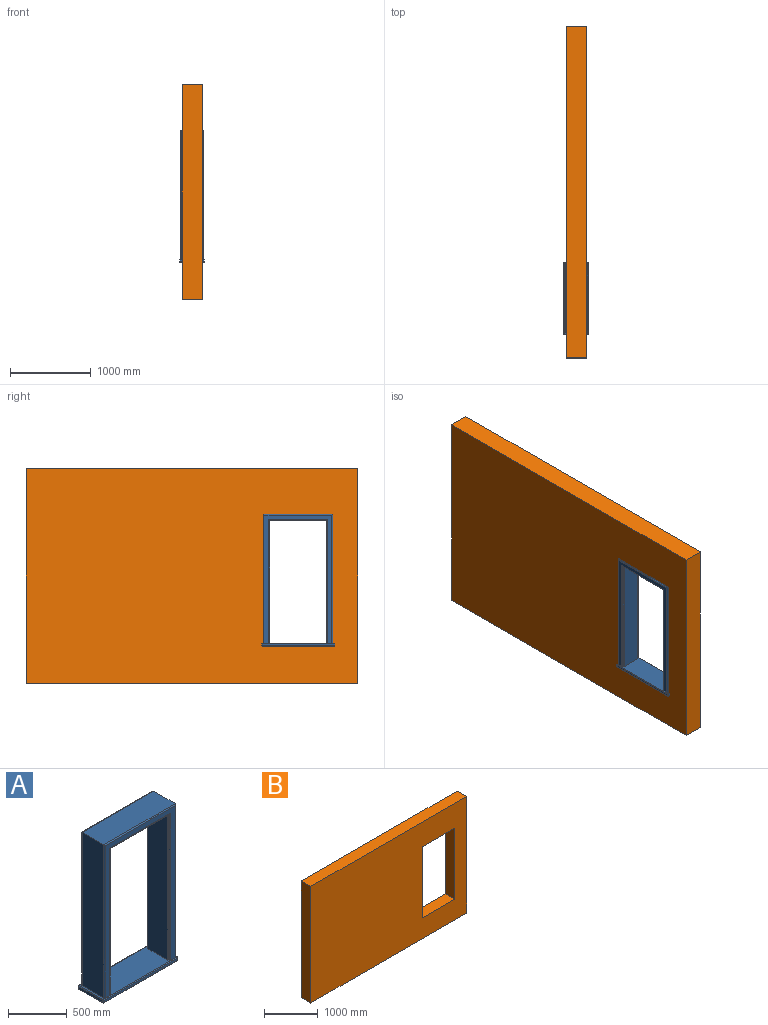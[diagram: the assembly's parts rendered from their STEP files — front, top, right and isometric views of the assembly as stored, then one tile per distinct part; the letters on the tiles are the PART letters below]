
ASSEMBLY  parts=2 mates=1
PART A: 54 faces, bbox 900x305x1630 mm
  f0: plane 888.12x293.12mm, normal (0,0,-1), area 260170.3mm2, adj f1,f2,f3,f4,f5,f6,f7,f8
  f1: torus R=4mm, axis (0,0,1), area 115.7mm2, adj f0,f2,f8,f9
  f2: cylinder r=6mm len=285mm, axis (0,1,0), area 2686.1mm2, adj f0,f1,f3,f10
  f3: torus R=4mm, axis (0,0,1), area 115.7mm2, adj f0,f2,f4,f11
  f4: cylinder r=6mm len=880mm, axis (1,0,0), area 8293.8mm2, adj f0,f3,f5,f12
  f5: torus R=4mm, axis (0,0,1), area 115.7mm2, adj f0,f4,f6,f13
  f6: cylinder r=6mm len=285mm, axis (0,-1,0), area 2686.1mm2, adj f0,f5,f7,f14
  f7: torus R=4mm, axis (0,0,1), area 115.7mm2, adj f0,f6,f8,f15
  f8: cylinder r=6mm len=880mm, axis (-1,0,0), area 8293.8mm2, adj f0,f1,f7,f16
  f9: cylinder r=10mm len=23mm, axis (0,0,1), area 361.3mm2, adj f1,f10,f16,f23
  f10: plane 285x23mm, normal (-1,0,0), area 6555mm2, adj f2,f9,f11,f24
  f11: cylinder r=10mm len=23mm, axis (0,0,1), area 361.3mm2, adj f3,f10,f12,f25
  f12: plane 880x23mm, normal (0,1,0), area 20240mm2, adj f4,f11,f13,f26
  f13: cylinder r=10mm len=23mm, axis (0,0,1), area 361.3mm2, adj f5,f12,f14,f27
  f14: plane 285x23mm, normal (1,0,0), area 6555mm2, adj f6,f13,f15,f28
  f15: cylinder r=10mm len=23mm, axis (0,0,1), area 361.3mm2, adj f7,f14,f16,f29
  f16: plane 880x23mm, normal (0,-1,0), area 20240mm2, adj f8,f9,f15,f30
  f17: cylinder r=10mm len=860mm, axis (1,0,0), area 13351.8mm2, adj f22,f35,f40,f41
  f18: cylinder r=10mm len=736mm, axis (-1,0,0), area 11404mm2, adj f19,f34,f41,f42
  f19: plane 716x10mm, normal (0,0,-1), area 7160mm2, adj f18,f33,f43,f44
  f20: plane 700x240mm, normal (0,0,-1), area 168000mm2, adj f32,f37,f44,f45
  f21: plane 716x10mm, normal (0,0,-1), area 7160mm2, adj f31,f37,f38,f47
  f22: plane 860x260mm, normal (0,0,1), area 223600mm2, adj f17,f36,f39,f50
  f23: torus R=4mm, axis (0,0,1), area 115.7mm2, adj f9,f24,f30,f52
  f24: cylinder r=6mm len=285mm, axis (0,-1,0), area 2686.1mm2, adj f10,f23,f25,f52
  f25: torus R=4mm, axis (0,0,1), area 115.7mm2, adj f11,f24,f26,f52
  f26: cylinder r=6mm len=880mm, axis (-1,0,0), area 8293.8mm2, adj f12,f25,f27,f52
  f27: torus R=4mm, axis (0,0,1), area 115.7mm2, adj f13,f26,f28,f52
  f28: cylinder r=6mm len=285mm, axis (0,1,0), area 2686.1mm2, adj f14,f27,f29,f52
  f29: torus R=4mm, axis (0,0,1), area 115.7mm2, adj f15,f28,f30,f52
  f30: cylinder r=6mm len=880mm, axis (1,0,0), area 8293.8mm2, adj f16,f23,f29,f52
  f31: plane 1523x10mm, normal (1,0,0), area 15230mm2, adj f21,f37,f46,f52
  f32: plane 1515x240mm, normal (1,0,0), area 363600mm2, adj f20,f37,f44,f52
  f33: plane 1523x10mm, normal (1,0,0), area 15230mm2, adj f19,f34,f44,f52
  f34: cylinder r=10mm len=1533mm, axis (0,0,-1), area 24001.8mm2, adj f18,f33,f41,f52
  f35: cylinder r=10mm len=1595mm, axis (0,0,1), area 24975.7mm2, adj f17,f36,f41,f52
  f36: plane 1595x260mm, normal (-1,0,0), area 414700mm2, adj f22,f35,f51,f52
  f37: plane 1523x716mm, normal (0,-1,0), area 29968mm2, adj f20,f21,f31,f32,f38,f45,f52
  f38: plane 1523x10mm, normal (-1,0,0), area 15230mm2, adj f21,f37,f48,f52
  f39: plane 1595x260mm, normal (1,0,0), area 414700mm2, adj f22,f40,f49,f52
  f40: cylinder r=10mm len=1595mm, axis (0,0,-1), area 24975.7mm2, adj f17,f39,f41,f52
  f41: plane 1585x840mm, normal (0,1,0), area 203112mm2, adj f17,f18,f34,f35,f40,f42,f52
  f42: cylinder r=10mm len=1533mm, axis (0,0,1), area 24001.8mm2, adj f18,f41,f43,f52
  f43: plane 1523x10mm, normal (-1,0,0), area 15230mm2, adj f19,f42,f44,f52
  f44: plane 1523x716mm, normal (0,1,0), area 29968mm2, adj f19,f20,f32,f33,f43,f45,f52
  f45: plane 1515x240mm, normal (-1,0,0), area 363600mm2, adj f20,f37,f44,f52
  f46: cylinder r=10mm len=1533mm, axis (0,0,1), area 24001.8mm2, adj f31,f47,f52,f53
  f47: cylinder r=10mm len=736mm, axis (1,0,0), area 11404mm2, adj f21,f46,f48,f53
  f48: cylinder r=10mm len=1533mm, axis (0,0,-1), area 24001.8mm2, adj f38,f47,f52,f53
  f49: cylinder r=10mm len=1595mm, axis (0,0,1), area 24975.7mm2, adj f39,f50,f52,f53
  f50: cylinder r=10mm len=860mm, axis (-1,0,0), area 13351.8mm2, adj f22,f49,f51,f53
  f51: cylinder r=10mm len=1595mm, axis (0,0,-1), area 24975.7mm2, adj f36,f50,f52,f53
  f52: plane 888.13x293.13mm, normal (0,0,1), area 216181.9mm2, adj f23,f24,f25,f26,f27,f28,f29,f30
  f53: plane 1585x840mm, normal (0,-1,0), area 203112mm2, adj f46,f47,f48,f49,f50,f51,f52
PART B: 10 faces, bbox 4098x250x2655 mm
  f0: plane 4098x250mm, normal (0,0,1), area 1024500mm2, adj f5,f6,f7,f8
  f1: plane 855x250mm, normal (0,0,1), area 213750mm2, adj f2,f4,f6,f8
  f2: plane 1620x250mm, normal (-1,0,0), area 405000mm2, adj f1,f3,f6,f8
  f3: plane 855x250mm, normal (0,0,-1), area 213750mm2, adj f2,f4,f6,f8
  f4: plane 1620x250mm, normal (1,0,0), area 405000mm2, adj f1,f3,f6,f8
  f5: plane 2655x250mm, normal (-1,0,0), area 663750mm2, adj f0,f6,f8,f9
  f6: plane 4098x2655mm, normal (0,-1,0), area 9495090mm2, adj f0,f1,f2,f3,f4,f5,f7,f9
  f7: plane 2655x250mm, normal (1,0,0), area 663750mm2, adj f0,f6,f8,f9
  f8: plane 4098x2655mm, normal (0,1,0), area 9495090mm2, adj f0,f1,f2,f3,f4,f5,f7,f9
  f9: plane 4098x250mm, normal (0,0,-1), area 1024500mm2, adj f5,f6,f7,f8
PLACE A rot(axis=(0,0,1),90deg) t=(-3609.59,2074.34,526.72)mm
PLACE B rot(axis=(0,0,-1),90deg) t=(-3484.59,5432.34,31.72)mm
MATE fastened A.f36 <-> B.f2  axis (0,-1,0) through (-3609.59,1644.34,2121.72)mm
